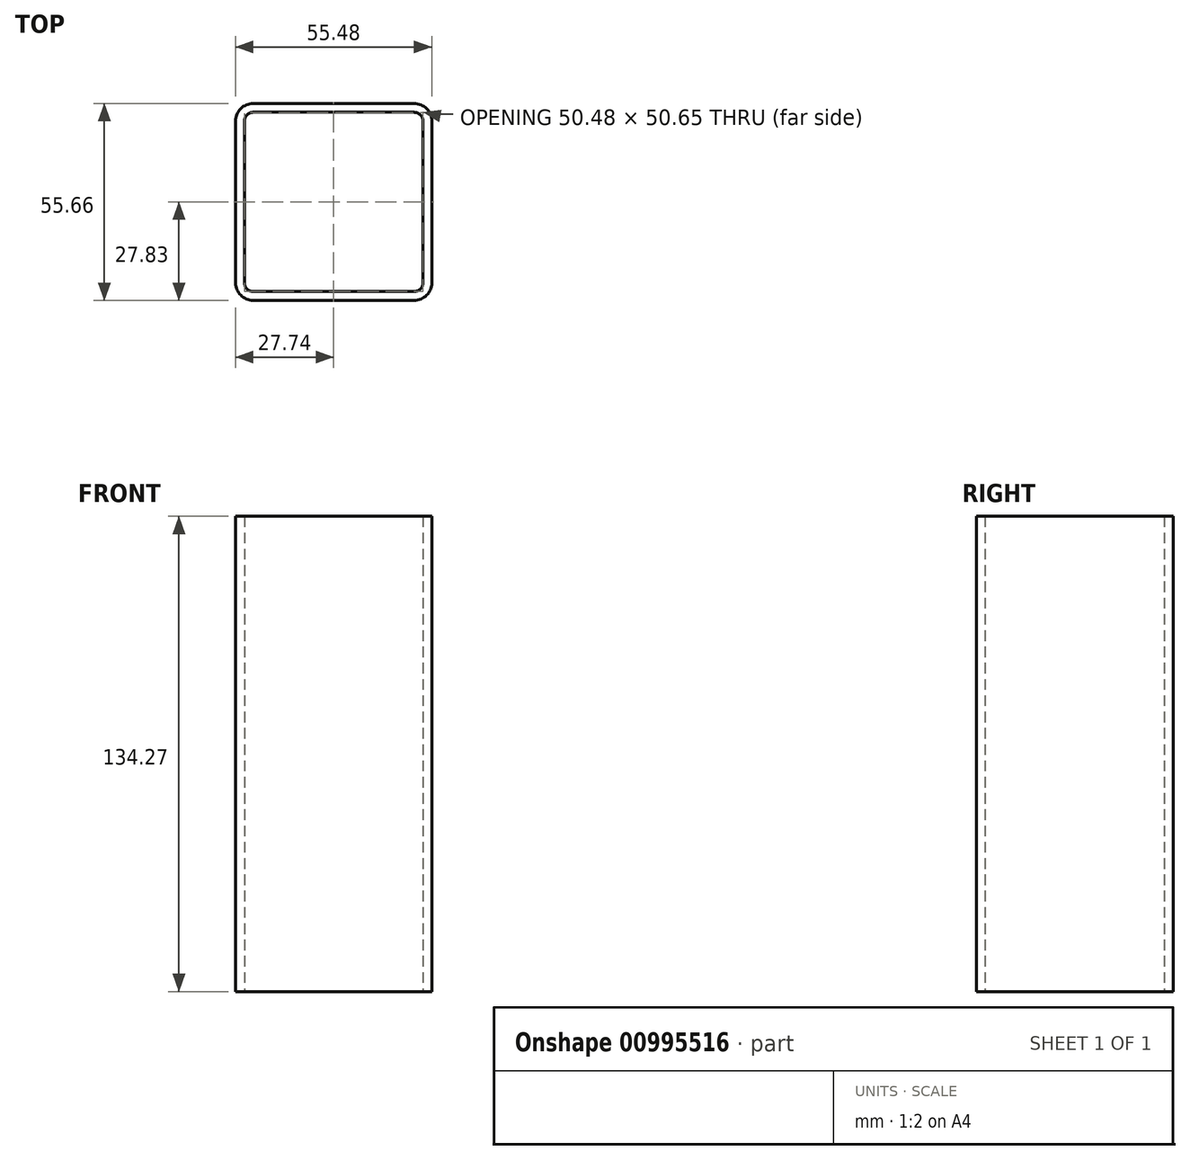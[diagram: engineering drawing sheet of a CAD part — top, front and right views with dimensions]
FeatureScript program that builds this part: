
annotation { "Feature Type Name" : "Feature", "Feature Type Description" : "" }
export const myFeature = defineFeature(function(context is Context, id is Id, definition is map)
    precondition{}
    {
        {
            var Q0;
            Q0=qCreatedBy(makeId("Top.planeOp"),FACE);
            var sketch = newSketch(context, id + "F0", { "sketchPlane" : qUnion([Q0])});
            skLineSegment(sketch, "E0.bottom", {"start": v(27.74, 27.83) * mm, "end": v(-27.74, 27.83) * mm});
            skLineSegment(sketch, "E0.top", {"start": v(27.74, -27.83) * mm, "end": v(-27.74, -27.83) * mm});
            skLineSegment(sketch, "E0.left", {"start": v(27.74, 27.83) * mm, "end": v(27.74, -27.83) * mm});
            skLineSegment(sketch, "E0.right", {"start": v(-27.74, 27.83) * mm, "end": v(-27.74, -27.83) * mm});
            skPoint(sketch, "E0.middle", {"position": v(0, 0) * mm});
            skSolve(sketch);
        }
        {
            var Q0;
            Q0=makeQuery(id+"F0.imprint","IMPRINT",FACE,{"disambiguationData":[TD([[makeQuery(id+"F0.imprint","IMPRINT",EDGE,{"derivedFrom":sQuery(id+"F0.wireOp",EDGE,"E0.bottom")}),1.0]])]});
            extrude(context, id + "F1", {"entities" : qUnion([Q0]), "depth" : 134.27 * mm, "offsetDistance" : 25 * mm});
        }
        {
            var Q0;
            Q0=makeQuery(id+"F1.opExtrude","SWEPT_EDGE",EDGE,{"disambiguationData":[OSD([sQuery(id+"F0.wireOp",EDGE,"E0.top"),sQuery(id+"F0.wireOp",EDGE,"E0.left")])]});
            var Q1;
            Q1=makeQuery(id+"F1.opExtrude","SWEPT_EDGE",EDGE,{"disambiguationData":[OSD([sQuery(id+"F0.wireOp",EDGE,"E0.bottom"),sQuery(id+"F0.wireOp",EDGE,"E0.left")])]});
            var Q2;
            Q2=makeQuery(id+"F1.opExtrude","SWEPT_EDGE",EDGE,{"disambiguationData":[OSD([sQuery(id+"F0.wireOp",EDGE,"E0.top"),sQuery(id+"F0.wireOp",EDGE,"E0.right")])]});
            var Q3;
            Q3=makeQuery(id+"F1.opExtrude","SWEPT_EDGE",EDGE,{"disambiguationData":[OSD([sQuery(id+"F0.wireOp",EDGE,"E0.bottom"),sQuery(id+"F0.wireOp",EDGE,"E0.right")])]});
            fillet(context, id + "F2", {"entities" : qUnion([Q0, Q1, Q2, Q3]), "radius" : 5 * mm, "tangentPropagation" : true, "allowEdgeOverflow" : false});
        }
        {
            var Q0;
            Q0=makeQuery(id+"F1.opExtrude","CAP_FACE",FACE,{"disambiguationData":[OSD([sQuery(id+"F0.wireOp",EDGE,"E0.bottom"),sQuery(id+"F0.wireOp",EDGE,"E0.top"),sQuery(id+"F0.wireOp",EDGE,"E0.left"),sQuery(id+"F0.wireOp",EDGE,"E0.right")])],"isStart":false});
            var Q1;
            Q1=makeQuery(id+"F1.opExtrude","CAP_FACE",FACE,{"disambiguationData":[OSD([sQuery(id+"F0.wireOp",EDGE,"E0.bottom"),sQuery(id+"F0.wireOp",EDGE,"E0.top"),sQuery(id+"F0.wireOp",EDGE,"E0.left"),sQuery(id+"F0.wireOp",EDGE,"E0.right")])],"isStart":true});
            shell(context, id + "F3", {"entities" : qUnion([Q0, Q1]), "thickness" : 2.5 * mm});
        }
    });
